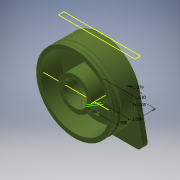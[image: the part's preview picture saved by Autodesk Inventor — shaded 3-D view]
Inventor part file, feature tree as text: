
AUTODESK INVENTOR PART (.ipt)
format: ipt  version: 2018 (Build 220112000, 112)  size: 348,160 bytes
history: native  units: in
note: dims shown in document units (in); Inventor stores cm internally (conversion verified against a paired STEP export)
features: sketch x17, extrude x13, reference x6, other x3, projected_geometry x2, revolve x1, mirror x1, fillet x1
ambient origin geometry x8: Origin, YZ Plane, XZ Plane, XY Plane, X Axis, Y Axis, Z Axis, Center Point
bodies: Solid1 (feature_tree)
feature tree (44):
  extrude  "Extrusion1"  Depth=3.5in
  extrude  "Extrusion2"  Depth=1.75in
  extrude  "Extrusion3"  Depth=0.25in TaperAngle=0.0deg
  extrude  "Extrusion4"  Depth=1.0in TaperAngle=0.0deg
  extrude  "Extrusion7"  Depth=1.5in TaperAngle=0.0deg
  revolve  "Revolution1"  [1 undecoded]
  sketch  "Sketch11"  dims[d26=1.0in d27=0.0in d28=0.1275in]
  sketch  "Sketch12"  dims[d31=0.75in d33=90.0deg]
  extrude  "Extrusion11"  Depth=0.1275in
  extrude  "Extrusion12"  TaperAngle=90.0deg  [1 undecoded]
  sketch  "Sketch15"  dims[d53=0.2953in d54=0.1181in]
  mirror  "Mirror2"
  extrude  "Extrusion14"  Depth=1.0in
  extrude  "Extrusion15"  Depth=3.5in
  extrude  "Extrusion16"  Depth=0.2953in
  extrude  "Extrusion17"  Depth=0.2953in
  extrude  "Extrusion18"  TaperAngle=15.0deg  [1 undecoded]
  extrude  "Extrusion19"  Depth=1.0in
  fillet  "Fillet1"  Radius=1.0in
  sketch  "Sketch1"  dims[d0=3.5in d1=3.5in]
  sketch  "Sketch2"  dims[d2=3.5in d3=1.75in]
  sketch  "Sketch3"  dims[d4=1.75in d5=0.25in d6=0.0in]
  sketch  "Sketch4"  dims[d8=0.0625in d9=1.0in d10=0.0in]
  sketch  "Sketch7"  dims[d11=1.125in d12=1.5in d13=0.0in]
  projected_geometry  "Projected Loop1"
  sketch  "Sketch8"  dims[d14=1.5in d15=1.0in d16=0.0in]
  projected_geometry  "Projected Loop4"
  sketch  "Sketch13"  dims[d43=1.0in d44=0.5in]
  sketch  "Sketch14"  dims[d45=0.0675in d46=3.5in]
  sketch  "Sketch16"  dims[d55=0.1181in d56=0.2953in]
  sketch  "Sketch17"  dims[d57=14.1732in d59=360.0deg d61=15.0deg]
  sketch  "Sketch18"  dims[d62=0.5256in d63=0.0in d64=0.2135in d69=1.0in d70=0.0in]
  reference  "Reference3"
  reference  "Reference4"
  sketch  "Sketch19"  dims[d71=1.25in]
  reference  "Reference5"
  reference  "Reference6"
  reference  "Reference7"
  reference  "Reference8"
  sketch  "Sketch20"  dims[d72=1.25in]
  sketch  "Sketch21"  dims[d73=1.25in d74=1.25in d75=2.375in d76=1.0in d77=0.3051in d78=0.6102in d79=0.0791in d82=3.125in d83=0.4685in d84=1.125in d85=1.0in d86=0.0in d87=0.05in d88=1.0in d89=0.0in d90=1.0in d91=0.0in d92=0.02in d93=0.1693in d94=0.0in d95=0.1181in d98=15.0deg d99=0.2953in d100=0.1181in d101=0.375in d102=0.375in d103=0.1693in d104=0.0in d105=0.1693in d106=0.0in d107=0.25in]
  parser-record x1  (decoder bookkeeping rows leaked as tree rows — omitted from the tree; the rows remain in map.json)
  other  "Assembly1.iam"
  other  "microServo-sg90:1"
note: 3 required parameter values undecoded (feature->parameter linkage not recoverable at this tier; creation-order binding heuristic only, values carry confidence <= 0.55)
note: 1 file-system path scrubbed to <path> (originals preserved in map.json)